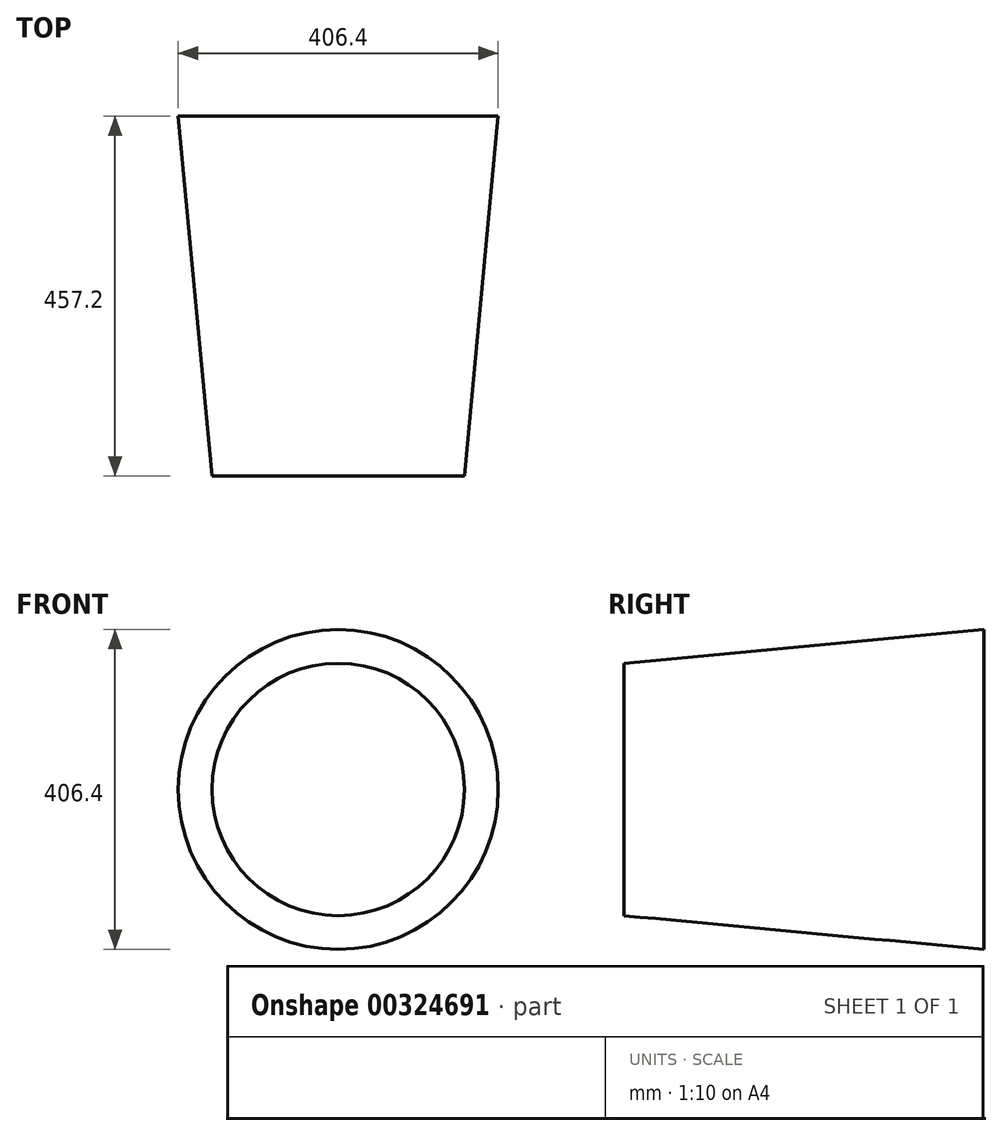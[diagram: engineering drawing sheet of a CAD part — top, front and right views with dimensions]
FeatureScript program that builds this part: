
annotation { "Feature Type Name" : "Feature", "Feature Type Description" : "" }
export const myFeature = defineFeature(function(context is Context, id is Id, definition is map)
    precondition{}
    {
        {
            var Q0;
            Q0=qCreatedBy(makeId("Front.planeOp"),FACE);
            var sketch = newSketch(context, id + "F0", { "sketchPlane" : qUnion([Q0])});
            skCircle(sketch, "E0", {"center": v(0, 0) * mm, "radius": 203.2 * mm});
            skSolve(sketch);
        }
        {
            var Q0;
            Q0=makeQuery(id+"F0.imprint","IMPRINT",FACE,{"disambiguationData":[TD([[makeQuery(id+"F0.imprint","IMPRINT",EDGE,{"derivedFrom":sQuery(id+"F0.wireOp",EDGE,"E0")}),1.0]])]});
            cPlane(context, id + "F1", {"entities" : qUnion([Q0]), "cplaneType" : CPlaneType.OFFSET, "offset" : 457.2 * mm, "width" : 152.4 * mm, "height" : 152.4 * mm});
        }
        {
            var Q0;
            Q0=qCreatedBy(id+"F1.planeOp",FACE);
            var sketch = newSketch(context, id + "F2", { "sketchPlane" : qUnion([Q0])});
            skCircle(sketch, "E1", {"center": v(0, 0) * mm, "radius": 160.34 * mm});
            skSolve(sketch);
        }
        {
            var Q0;
            Q0=makeQuery(id+"F2.imprint","IMPRINT",FACE,{"disambiguationData":[TD([[makeQuery(id+"F2.imprint","IMPRINT",EDGE,{"derivedFrom":sQuery(id+"F2.wireOp",EDGE,"E1")}),1.0]])]});
            var Q1;
            Q1=makeQuery(id+"F0.imprint","IMPRINT",FACE,{"disambiguationData":[TD([[makeQuery(id+"F0.imprint","IMPRINT",EDGE,{"derivedFrom":sQuery(id+"F0.wireOp",EDGE,"E0")}),1.0]])]});
            loft(context, id + "F3", {"sheetProfilesArray" : [{ "sheetProfileEntities" : qUnion([Q0]) }, { "sheetProfileEntities" : qUnion([Q1]) }]});
        }
    });
